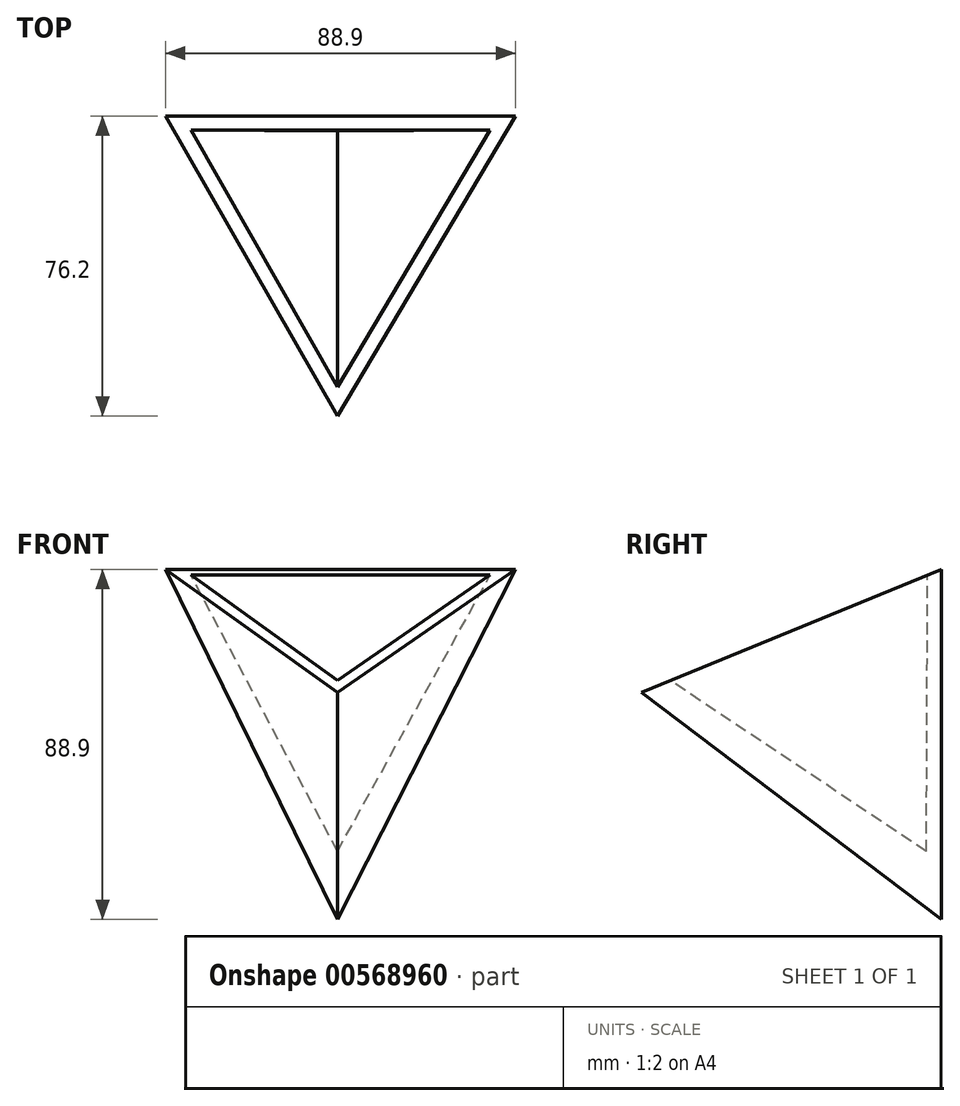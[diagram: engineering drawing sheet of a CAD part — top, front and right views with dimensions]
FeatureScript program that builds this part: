
annotation { "Feature Type Name" : "Feature", "Feature Type Description" : "" }
export const myFeature = defineFeature(function(context is Context, id is Id, definition is map)
    precondition{}
    {
        {
            var Q0;
            Q0=qCreatedBy(makeId("Front.planeOp"),FACE);
            var sketch = newSketch(context, id + "F0", { "sketchPlane" : qUnion([Q0])});
            skLineSegment(sketch, "E0", {"start": v(-20.85, -65.12) * mm, "end": v(-64.53, 23.78) * mm});
            skLineSegment(sketch, "E1", {"start": v(-64.53, 23.78) * mm, "end": v(24.37, 23.78) * mm});
            skLineSegment(sketch, "E2", {"start": v(24.37, 23.78) * mm, "end": v(-20.85, -65.12) * mm});
            skSolve(sketch);
        }
        {
            var Q0;
            Q0=qCreatedBy(makeId("Front.planeOp"),FACE);
            cPlane(context, id + "F1", {"entities" : qUnion([Q0]), "cplaneType" : CPlaneType.OFFSET, "offset" : 76.2 * mm, "width" : 152.4 * mm, "height" : 152.4 * mm});
        }
        {
            var Q0;
            Q0=qCreatedBy(id+"F1.planeOp",FACE);
            var sketch = newSketch(context, id + "F2", { "sketchPlane" : qUnion([Q0])});
            skPoint(sketch, "E3", {"position": v(-20.85, -7.43) * mm});
            skSolve(sketch);
        }
        {
            var Q0;
            Q0=makeQuery(id+"F0.imprint","IMPRINT",FACE,{"disambiguationData":[TD([[makeQuery(id+"F0.imprint","IMPRINT",EDGE,{"derivedFrom":sQuery(id+"F0.wireOp",EDGE,"E0")}),-1.0]])]});
            var Q1;
            Q1=sQuery(id+"F2.wireOp",VERTEX,"E3");
            loft(context, id + "F3", {"sheetProfilesArray" : [{ "sheetProfileEntities" : qUnion([Q0]) }, { "sheetProfileEntities" : qUnion([Q1]) }]});
        }
        {
            var Q0;
            {var subQ0=sQuery(id+"F0.wireOp",EDGE,"E1");var subQ1=sQuery(id+"F0.wireOp",EDGE,"E2");var subQ2=sQuery(id+"F0.wireOp",EDGE,"E0");Q0=makeQuery(id+"F3.opLoft","SWEPT_FACE",FACE,{"disambiguationData":[OSD([subQ2,subQ0,subQ1]),TDD([makeQuery(id+"F0.imprint","INTERSECT",VERTEX,{"derivedFrom":[subQ2,subQ0]}),makeQuery(id+"F0.imprint","INTERSECT",VERTEX,{"derivedFrom":[subQ0,subQ1]}),makeQuery(id+"F0.imprint","IMPRINT",EDGE,{"derivedFrom":subQ0})])]});}
            var sketch = newSketch(context, id + "F4", { "sketchPlane" : qUnion([Q0])});
            skLineSegment(sketch, "E4", {"start": v(-58.08, 5.2) * mm, "end": v(-20.85, -65.42) * mm});
            skLineSegment(sketch, "E5", {"start": v(17.93, 5.2) * mm, "end": v(-20.85, -65.42) * mm});
            skLineSegment(sketch, "E6", {"start": v(17.93, 5.2) * mm, "end": v(-58.08, 5.2) * mm});
            skSolve(sketch);
        }
        {
            var Q0;
            Q0=qCreatedBy(makeId("Front.planeOp"),FACE);
            cPlane(context, id + "F5", {"entities" : qUnion([Q0]), "cplaneType" : CPlaneType.OFFSET, "offset" : 3.8 * mm, "width" : 152.4 * mm, "height" : 152.4 * mm});
        }
        {
            var Q0;
            Q0=qCreatedBy(id+"F5.planeOp",FACE);
            var sketch = newSketch(context, id + "F6", { "sketchPlane" : qUnion([Q0])});
            skPoint(sketch, "E7", {"position": v(-20.85, -47.86) * mm});
            skSolve(sketch);
        }
        {
            var Q1;
            Q1=sQuery(id+"F6.wireOp",VERTEX,"E7");
            var Q2;
            Q2=makeQuery(id+"F4.imprint","IMPRINT",FACE,{"disambiguationData":[TD([[makeQuery(id+"F4.imprint","IMPRINT",EDGE,{"derivedFrom":sQuery(id+"F4.wireOp",EDGE,"E4")}),1.0]])]});
            loft(context, id + "F7", {"operationType" : NewBodyOperationType.REMOVE, "sheetProfilesArray" : [{ "sheetProfileEntities" : qUnion([Q1]) }, { "sheetProfileEntities" : qUnion([Q2]) }]});
        }
    });
